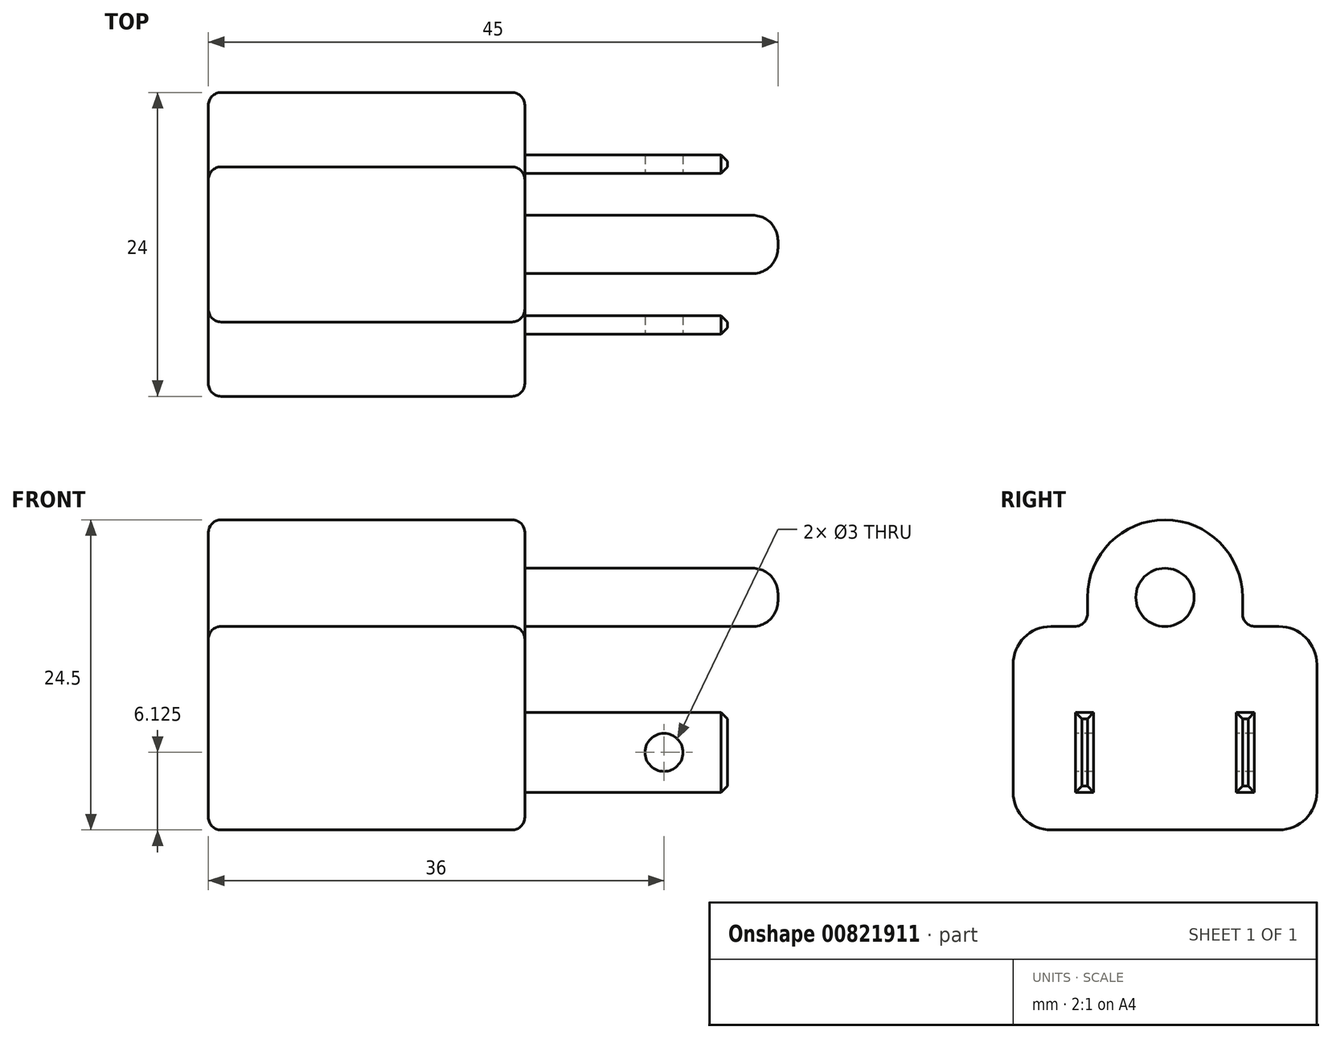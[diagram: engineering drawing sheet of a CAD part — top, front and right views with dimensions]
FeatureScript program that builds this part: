
annotation { "Feature Type Name" : "Feature", "Feature Type Description" : "" }
export const myFeature = defineFeature(function(context is Context, id is Id, definition is map)
    precondition{}
    {
        {
            var Q0;
            Q0=qCreatedBy(makeId("Right.planeOp"),FACE);
            var sketch = newSketch(context, id + "F0", { "sketchPlane" : qUnion([Q0])});
            skLineSegment(sketch, "E0.bottom", {"start": v(9, -12.25) * mm, "end": v(-9, -12.25) * mm});
            skLineSegment(sketch, "E0.left", {"start": v(12, -9.25) * mm, "end": v(12, 0.82) * mm});
            skLineSegment(sketch, "E0.right", {"start": v(-12, -9.25) * mm, "end": v(-12, 0.82) * mm});
            skPoint(sketch, "E0.middle", {"position": v(0, 0) * mm});
            skLineSegment(sketch, "E1.bottom", {"start": v(-5.62, -9.27) * mm, "end": v(-7.07, -9.27) * mm, "construction": true});
            skLineSegment(sketch, "E1.top", {"start": v(-5.62, -2.97) * mm, "end": v(-7.07, -2.97) * mm, "construction": true});
            skLineSegment(sketch, "E1.left", {"start": v(-5.62, -9.27) * mm, "end": v(-5.62, -2.97) * mm, "construction": true});
            skLineSegment(sketch, "E1.right", {"start": v(-7.07, -9.28) * mm, "end": v(-7.07, -2.97) * mm, "construction": true});
            skPoint(sketch, "E1.middle", {"position": v(-6.35, -6.12) * mm});
            skLineSegment(sketch, "E2.MirrorCS", {"start": v(5.62, -9.27) * mm, "end": v(7.07, -9.27) * mm, "construction": true});
            skLineSegment(sketch, "E3.MirrorCS", {"start": v(5.62, -2.97) * mm, "end": v(7.07, -2.97) * mm, "construction": true});
            skPoint(sketch, "E4.MirrorP", {"position": v(6.35, -6.12) * mm});
            skLineSegment(sketch, "E5.MirrorCS", {"start": v(7.07, -9.28) * mm, "end": v(7.07, -2.97) * mm, "construction": true});
            skLineSegment(sketch, "E6.MirrorCS", {"start": v(5.62, -9.27) * mm, "end": v(5.62, -2.97) * mm, "construction": true});
            skCircle(sketch, "E7", {"center": v(0, 6.12) * mm, "radius": 2.3 * mm, "construction": true});
            skLineSegment(sketch, "E8", {"start": v(-9, 3.83) * mm, "end": v(-6.12, 3.83) * mm});
            skArc(sketch, "E9", {"start": v(6.13, 6.12) * mm, "mid": v(0, 12.25) * mm, "end": v(-6.12, 6.13) * mm});
            skLineSegment(sketch, "E10", {"start": v(-6.12, 6.12) * mm, "end": v(-6.12, 3.83) * mm});
            skLineSegment(sketch, "E11.MirrorCS", {"start": v(6.12, 6.12) * mm, "end": v(6.12, 3.83) * mm});
            skLineSegment(sketch, "E12.trimOffspring", {"start": v(6.12, 3.83) * mm, "end": v(9, 3.83) * mm});
            skPoint(sketch, "E13", {"position": v(0, 12.25) * mm});
            skArc(sketch, "E14.filletArc", {"start": v(-9, 3.82) * mm, "mid": v(-11.12, 2.95) * mm, "end": v(-12, 0.83) * mm});
            skArc(sketch, "E15.filletArc", {"start": v(12, 0.82) * mm, "mid": v(11.12, 2.95) * mm, "end": v(9, 3.82) * mm});
            skArc(sketch, "E16.filletArc", {"start": v(9, -12.25) * mm, "mid": v(11.12, -11.37) * mm, "end": v(12, -9.25) * mm});
            skArc(sketch, "E17.filletArc", {"start": v(-12, -9.25) * mm, "mid": v(-11.12, -11.37) * mm, "end": v(-9, -12.25) * mm});
            skPoint(sketch, "E18", {"position": v(0, -12.25) * mm});
            skSolve(sketch);
        }
        {
            var Q0;
            Q0 = qSketchRegion(id + "F0", true);
            extrude(context, id + "F1", {"entities" : qUnion([Q0]), "endBound" : BoundingType.SYMMETRIC, "depth" : 25 * mm, "offsetDistance" : 25 * mm});
        }
        {
            var Q0;
            Q0=qCreatedBy(makeId("Right.planeOp"),FACE);
            var sketch = newSketch(context, id + "F2", { "sketchPlane" : qUnion([Q0])});
            skPoint(sketch, "E19.3", {"position": v(0, 0) * mm});
            skLineSegment(sketch, "E19.4", {"start": v(-5.62, -9.27) * mm, "end": v(-7.07, -9.27) * mm});
            skLineSegment(sketch, "E19.5", {"start": v(-5.62, -2.97) * mm, "end": v(-7.07, -2.97) * mm});
            skLineSegment(sketch, "E19.6", {"start": v(-5.62, -9.27) * mm, "end": v(-5.62, -2.97) * mm});
            skLineSegment(sketch, "E19.7", {"start": v(-7.07, -9.28) * mm, "end": v(-7.07, -2.97) * mm});
            skPoint(sketch, "E19.8", {"position": v(-6.35, -6.12) * mm});
            skLineSegment(sketch, "E19.9", {"start": v(5.62, -9.27) * mm, "end": v(7.07, -9.27) * mm});
            skLineSegment(sketch, "E19.10", {"start": v(5.62, -2.97) * mm, "end": v(7.07, -2.97) * mm});
            skPoint(sketch, "E19.11", {"position": v(6.35, -6.12) * mm});
            skLineSegment(sketch, "E19.12", {"start": v(7.07, -9.28) * mm, "end": v(7.07, -2.97) * mm});
            skLineSegment(sketch, "E19.13", {"start": v(5.62, -9.27) * mm, "end": v(5.62, -2.97) * mm});
            skCircle(sketch, "E19.14", {"center": v(0, 6.12) * mm, "radius": 2.3 * mm});
            skSolve(sketch);
        }
        {
            var Q0;
            Q0 = qSketchRegion(id + "F2", true);
            extrude(context, id + "F3", {"entities" : qUnion([Q0]), "operationType" : NewBodyOperationType.ADD, "depth" : 28.5 * mm, "offsetDistance" : 25 * mm});
        }
        {
            var Q0;
            Q0=qCreatedBy(makeId("Front.planeOp"),FACE);
            var sketch = newSketch(context, id + "F4", { "sketchPlane" : qUnion([Q0])});
            skCircle(sketch, "E20", {"center": v(23.5, -6.12) * mm, "radius": 1.5 * mm});
            skLineSegment(sketch, "E21.0.0", {"start": v(28.5, -2.97) * mm, "end": v(12.5, -2.97) * mm, "construction": true});
            skLineSegment(sketch, "E21.0.1", {"start": v(12.5, -2.97) * mm, "end": v(12.5, -9.27) * mm, "construction": true});
            skLineSegment(sketch, "E21.0.2", {"start": v(12.5, -9.28) * mm, "end": v(28.5, -9.28) * mm, "construction": true});
            skLineSegment(sketch, "E21.0.3", {"start": v(28.5, -9.28) * mm, "end": v(28.5, -2.97) * mm, "construction": true});
            skPoint(sketch, "E22", {"position": v(28.5, -6.12) * mm});
            skSolve(sketch);
        }
        {
            var Q0;
            Q0 = qSketchRegion(id + "F4", true);
            extrude(context, id + "F5", {"entities" : qUnion([Q0]), "operationType" : NewBodyOperationType.REMOVE, "endBound" : BoundingType.SYMMETRIC, "oppositeDirection" : true, "depth" : 25 * mm, "offsetDistance" : 25 * mm});
        }
        {
            var Q0;
            Q0=makeQuery(id+"F3.opExtrude","CAP_FACE",FACE,{"disambiguationData":[OSD([sQuery(id+"F2.wireOp",EDGE,"E19.4"),sQuery(id+"F2.wireOp",EDGE,"E19.5"),sQuery(id+"F2.wireOp",EDGE,"E19.6"),sQuery(id+"F2.wireOp",EDGE,"E19.7")])],"isStart":false});
            var Q1;
            Q1=makeQuery(id+"F3.opExtrude","CAP_FACE",FACE,{"disambiguationData":[OSD([sQuery(id+"F2.wireOp",EDGE,"E19.9"),sQuery(id+"F2.wireOp",EDGE,"E19.10"),sQuery(id+"F2.wireOp",EDGE,"E19.12"),sQuery(id+"F2.wireOp",EDGE,"E19.13")])],"isStart":false});
            chamfer(context, id + "F6", {"entities" : qUnion([Q0, Q1]), "width" : 0.5 * mm, "tangentPropagation" : true});
        }
        {
            var Q0;
            Q0=makeQuery(id+"F3.opExtrude","CAP_FACE",FACE,{"disambiguationData":[OSD([sQuery(id+"F2.wireOp",EDGE,"E19.14")])],"isStart":false});
            var sketch = newSketch(context, id + "F7", { "sketchPlane" : qUnion([Q0])});
            skCircle(sketch, "E23.0", {"center": v(0, 6.12) * mm, "radius": 2.3 * mm});
            skSolve(sketch);
        }
        {
            var Q0;
            Q0 = qSketchRegion(id + "F7", true);
            extrude(context, id + "F8", {"entities" : qUnion([Q0]), "operationType" : NewBodyOperationType.ADD, "depth" : 4 * mm, "offsetDistance" : 25 * mm});
        }
        {
            var Q0;
            Q0=makeQuery(id+"F8.opExtrude","CAP_EDGE",EDGE,{"disambiguationData":[OSD([sQuery(id+"F7.wireOp",EDGE,"E23.0")])],"isStart":false});
            fillet(context, id + "F9", {"entities" : qUnion([Q0]), "radius" : 2 * mm, "tangentPropagation" : true, "allowEdgeOverflow" : false});
        }
        {
            var Q0;
            Q0=makeQuery(id+"F1.opExtrude","CAP_EDGE",EDGE,{"disambiguationData":[OSD([sQuery(id+"F0.wireOp",EDGE,"E9")])],"isStart":false});
            var Q1;
            Q1=makeQuery(id+"F1.opExtrude","CAP_EDGE",EDGE,{"disambiguationData":[OSD([sQuery(id+"F0.wireOp",EDGE,"E12.trimOffspring")])],"isStart":false});
            var Q2;
            Q2=makeQuery(id+"F1.opExtrude","CAP_EDGE",EDGE,{"disambiguationData":[OSD([sQuery(id+"F0.wireOp",EDGE,"E16.filletArc")])],"isStart":true});
            var Q3;
            Q3=makeQuery(id+"F1.opExtrude","CAP_EDGE",EDGE,{"disambiguationData":[OSD([sQuery(id+"F0.wireOp",EDGE,"E9")])],"isStart":true});
            var Q4;
            Q4=makeQuery(id+"F1.opExtrude","SWEPT_EDGE",EDGE,{"disambiguationData":[OSD([sQuery(id+"F0.wireOp",EDGE,"E8"),sQuery(id+"F0.wireOp",EDGE,"E10")])]});
            var Q5;
            Q5=makeQuery(id+"F1.opExtrude","SWEPT_EDGE",EDGE,{"disambiguationData":[OSD([sQuery(id+"F0.wireOp",EDGE,"E11.MirrorCS"),sQuery(id+"F0.wireOp",EDGE,"E12.trimOffspring")])]});
            fillet(context, id + "F10", {"entities" : qUnion([Q0, Q1, Q2, Q3, Q4, Q5]), "radius" : 1 * mm, "tangentPropagation" : true, "allowEdgeOverflow" : false});
        }
    });
